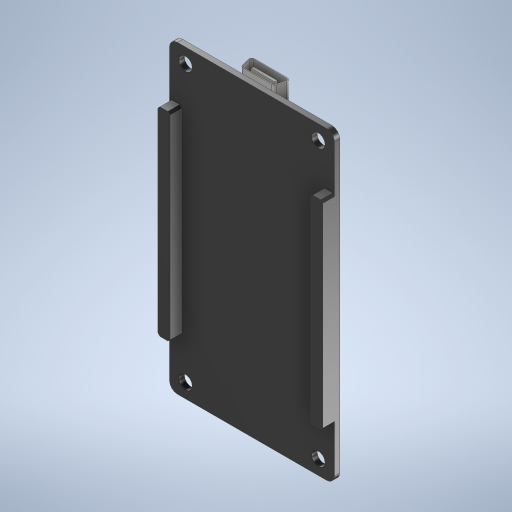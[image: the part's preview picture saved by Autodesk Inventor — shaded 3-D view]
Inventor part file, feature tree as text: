
AUTODESK INVENTOR PART (.ipt)
format: ipt  version: 2023 (Build 270158000, 158)  size: 446,464 bytes
history: native  units: mm
features: extrude x8, sketch x7, fillet x2, projected_geometry x2, other x1, mirror x1
ambient origin geometry x8: Origin, YZ Plane, XZ Plane, XY Plane, X Axis, Y Axis, Z Axis, Center Point
bodies: Body1 (feature_tree)
feature tree (21):
  other  "솔리드1"
  extrude  "돌출1"  Depth=31.2mm
  extrude  "돌출2"  Depth=57.6mm
  extrude  "돌출3"  Depth=2.5mm
  extrude  "돌출4"  Depth=25.1mm
  sketch  "스케치5"
  extrude  "돌출5"  Depth=1.0mm TaperAngle=0.0deg
  extrude  "돌출6"  Depth=1.5mm
  fillet  "모깎기1"  Radius=7.6mm
  extrude  "돌출7"  Depth=2.6mm
  extrude  "돌출8"  TaperAngle=15.0deg  [1 undecoded]
  mirror  "미러1"
  fillet  "모깎기2"  Radius=0.5mm
  sketch  "스케치1"
  sketch  "스케치2"
  sketch  "스케치3"
  projected_geometry  "투영된 루프1"
  sketch  "스케치4"
  projected_geometry  "투영된 루프2"
  sketch  "스케치6"
  sketch  "스케치7"
note: 1 required parameter value undecoded (feature->parameter linkage not recoverable at this tier; creation-order binding heuristic only, values carry confidence <= 0.55)
